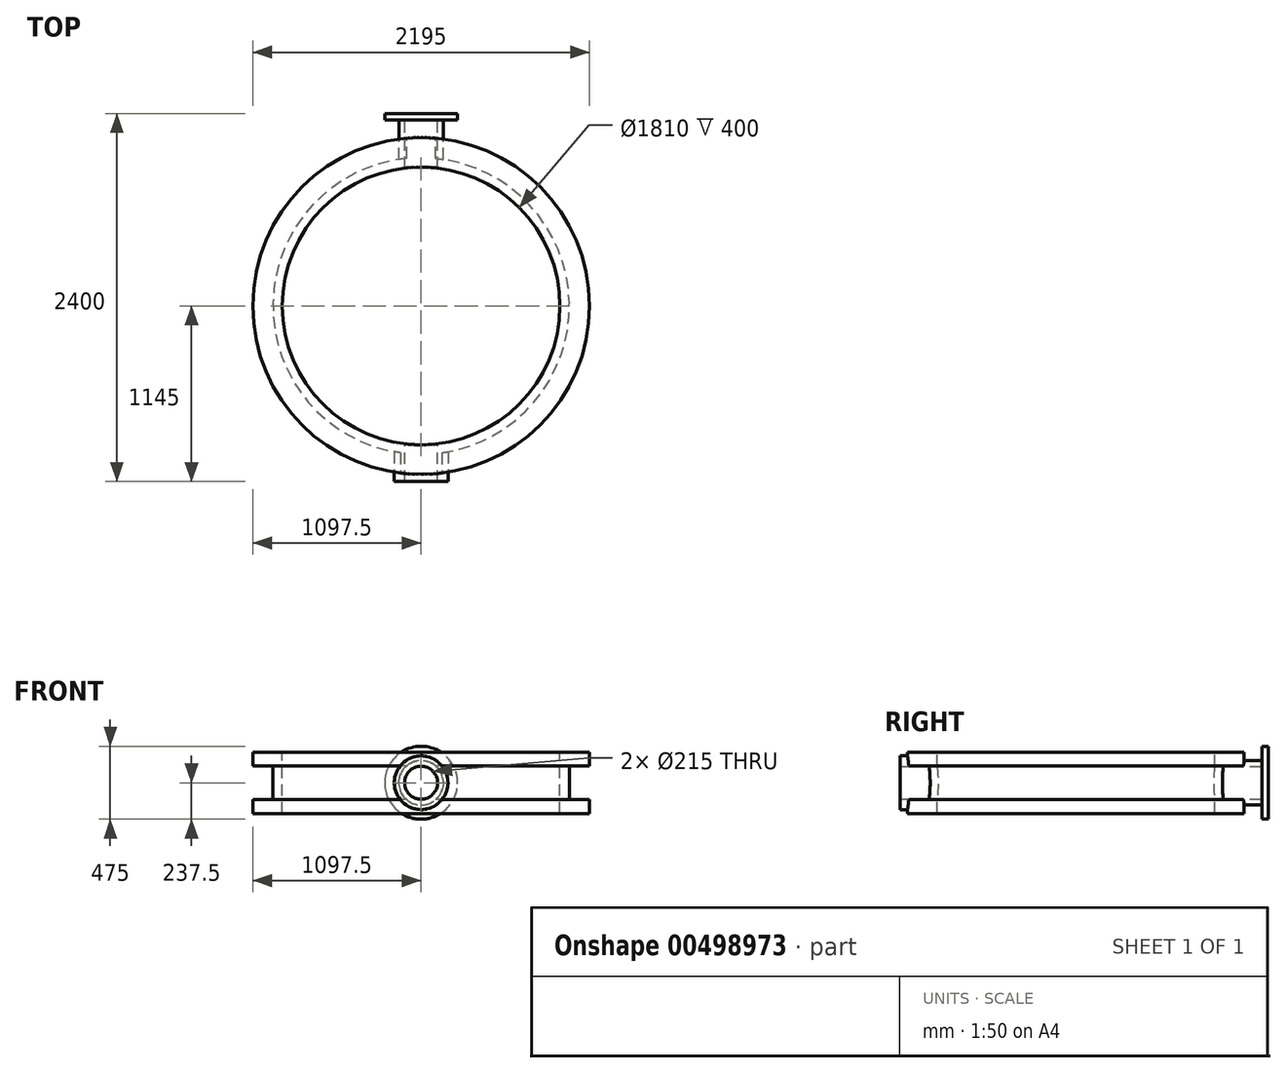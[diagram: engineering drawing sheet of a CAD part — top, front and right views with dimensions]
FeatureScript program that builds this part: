
annotation { "Feature Type Name" : "Feature", "Feature Type Description" : "" }
export const myFeature = defineFeature(function(context is Context, id is Id, definition is map)
    precondition{}
    {
        {
            var Q0;
            Q0=qCreatedBy(makeId("Top.planeOp"),FACE);
            var sketch = newSketch(context, id + "F0", { "sketchPlane" : qUnion([Q0])});
            skCircle(sketch, "E0", {"center": v(0, 0) * mm, "radius": 1097.5 * mm});
            skSolve(sketch);
        }
        {
            var Q0;
            Q0 = qSketchRegion(id + "F0", true);
            extrude(context, id + "F1", {"entities" : qUnion([Q0]), "depth" : 89 * mm, "offsetDistance" : 25 * mm});
        }
        {
            var Q0;
            Q0=makeQuery(id+"F1.opExtrude","CAP_FACE",FACE,{"disambiguationData":[OSD([sQuery(id+"F0.wireOp",EDGE,"E0")])],"isStart":true});
            var sketch = newSketch(context, id + "F2", { "sketchPlane" : qUnion([Q0])});
            skCircle(sketch, "E1", {"center": v(0, 0) * mm, "radius": 966 * mm});
            skSolve(sketch);
        }
        {
            var Q0;
            Q0 = qSketchRegion(id + "F2", true);
            extrude(context, id + "F3", {"entities" : qUnion([Q0]), "operationType" : NewBodyOperationType.ADD, "oppositeDirection" : true, "depth" : 400 * mm, "offsetDistance" : 25 * mm});
        }
        {
            var Q0;
            Q0=makeQuery(id+"F3.opExtrude","CAP_FACE",FACE,{"disambiguationData":[OSD([sQuery(id+"F2.wireOp",EDGE,"E1")])],"isStart":false});
            var sketch = newSketch(context, id + "F4", { "sketchPlane" : qUnion([Q0])});
            skCircle(sketch, "E2", {"center": v(0, 0) * mm, "radius": 1097.5 * mm});
            skSolve(sketch);
        }
        {
            var Q0;
            Q0 = qSketchRegion(id + "F4", true);
            extrude(context, id + "F5", {"entities" : qUnion([Q0]), "operationType" : NewBodyOperationType.ADD, "oppositeDirection" : true, "depth" : 89 * mm, "offsetDistance" : 25 * mm});
        }
        {
            var Q0;
            Q0=makeQuery(id+"F5.boolean.opBoolean","MERGE",FACE,{"derivedFrom":[makeQuery(id+"F3.opExtrude","CAP_FACE",FACE,{"disambiguationData":[OSD([sQuery(id+"F2.wireOp",EDGE,"E1")])],"isStart":false}),makeQuery(id+"F5.opExtrude","CAP_FACE",FACE,{"disambiguationData":[OSD([sQuery(id+"F4.wireOp",EDGE,"E2")])],"isStart":true})]});
            var sketch = newSketch(context, id + "F6", { "sketchPlane" : qUnion([Q0])});
            skCircle(sketch, "E3", {"center": v(0, 0) * mm, "radius": 905 * mm});
            skSolve(sketch);
        }
        {
            var Q0;
            Q0 = qSketchRegion(id + "F6", true);
            extrude(context, id + "F7", {"entities" : qUnion([Q0]), "operationType" : NewBodyOperationType.REMOVE, "endBound" : BoundingType.UP_TO_NEXT, "oppositeDirection" : true, "depth" : 25 * mm, "offsetDistance" : 25 * mm});
        }
        {
            var Q0;
            Q0=qCreatedBy(makeId("Front.planeOp"),FACE);
            cPlane(context, id + "F8", {"entities" : qUnion([Q0]), "cplaneType" : CPlaneType.OFFSET, "offset" : 1145 * mm, "width" : 150 * mm, "height" : 150 * mm});
        }
        {
            var Q0;
            Q0=qCreatedBy(id+"F8.planeOp",FACE);
            var sketch = newSketch(context, id + "F9", { "sketchPlane" : qUnion([Q0])});
            skCircle(sketch, "E4", {"center": v(0, 200) * mm, "radius": 175 * mm});
            skSolve(sketch);
        }
        {
            var Q0;
            Q0 = qSketchRegion(id + "F9", true);
            extrude(context, id + "F10", {"entities" : qUnion([Q0]), "operationType" : NewBodyOperationType.ADD, "endBound" : BoundingType.UP_TO_NEXT, "oppositeDirection" : true, "depth" : 25 * mm, "offsetDistance" : 25 * mm});
        }
        {
            var Q0;
            Q0=qCreatedBy(makeId("Front.planeOp"),FACE);
            cPlane(context, id + "F11", {"entities" : qUnion([Q0]), "cplaneType" : CPlaneType.OFFSET, "offset" : 1255 * mm, "oppositeDirection" : true, "width" : 150 * mm, "height" : 150 * mm});
        }
        {
            var Q0;
            Q0=qCreatedBy(id+"F11.planeOp",FACE);
            var sketch = newSketch(context, id + "F12", { "sketchPlane" : qUnion([Q0])});
            skCircle(sketch, "E5", {"center": v(0, 200) * mm, "radius": 237.5 * mm});
            skSolve(sketch);
        }
        {
            var Q0;
            Q0 = qSketchRegion(id + "F12", true);
            extrude(context, id + "F13", {"entities" : qUnion([Q0]), "depth" : 43 * mm, "offsetDistance" : 25 * mm});
        }
        {
            var Q0;
            Q0=makeQuery(id+"F13.opExtrude","CAP_FACE",FACE,{"disambiguationData":[OSD([sQuery(id+"F12.wireOp",EDGE,"E5")])],"isStart":false});
            var sketch = newSketch(context, id + "F14", { "sketchPlane" : qUnion([Q0])});
            skCircle(sketch, "E6", {"center": v(0, 200) * mm, "radius": 145 * mm});
            skSolve(sketch);
        }
        {
            var Q0;
            Q0 = qSketchRegion(id + "F14", true);
            var Q1;
            Q1=makeQuery(id+"F13.opExtrude","CAP_FACE",FACE,{"disambiguationData":[OSD([sQuery(id+"F12.wireOp",EDGE,"E5")])],"isStart":true});
            extrude(context, id + "F15", {"entities" : qUnion([Q0, Q1]), "operationType" : NewBodyOperationType.ADD, "endBound" : BoundingType.UP_TO_NEXT, "depth" : 25 * mm, "offsetDistance" : 25 * mm});
        }
        {
            var Q0;
            Q0=makeQuery(id+"F13.opExtrude","CAP_FACE",FACE,{"disambiguationData":[OSD([sQuery(id+"F12.wireOp",EDGE,"E5")])],"isStart":true});
            var sketch = newSketch(context, id + "F16", { "sketchPlane" : qUnion([Q0])});
            skCircle(sketch, "E7", {"center": v(0, 200) * mm, "radius": 107.5 * mm});
            skSolve(sketch);
        }
        {
            var Q0;
            Q0 = qSketchRegion(id + "F16", true);
            var Q1;
            Q1=makeQuery(id+"F10.opExtrude","CAP_FACE",FACE,{"disambiguationData":[OSD([sQuery(id+"F9.wireOp",EDGE,"E4")])],"isStart":true});
            extrude(context, id + "F17", {"entities" : qUnion([Q0]), "operationType" : NewBodyOperationType.REMOVE, "endBound" : BoundingType.UP_TO_SURFACE, "oppositeDirection" : true, "depth" : 25 * mm, "endBoundEntityFace" : qUnion([Q1]), "offsetDistance" : 25 * mm});
        }
    });
